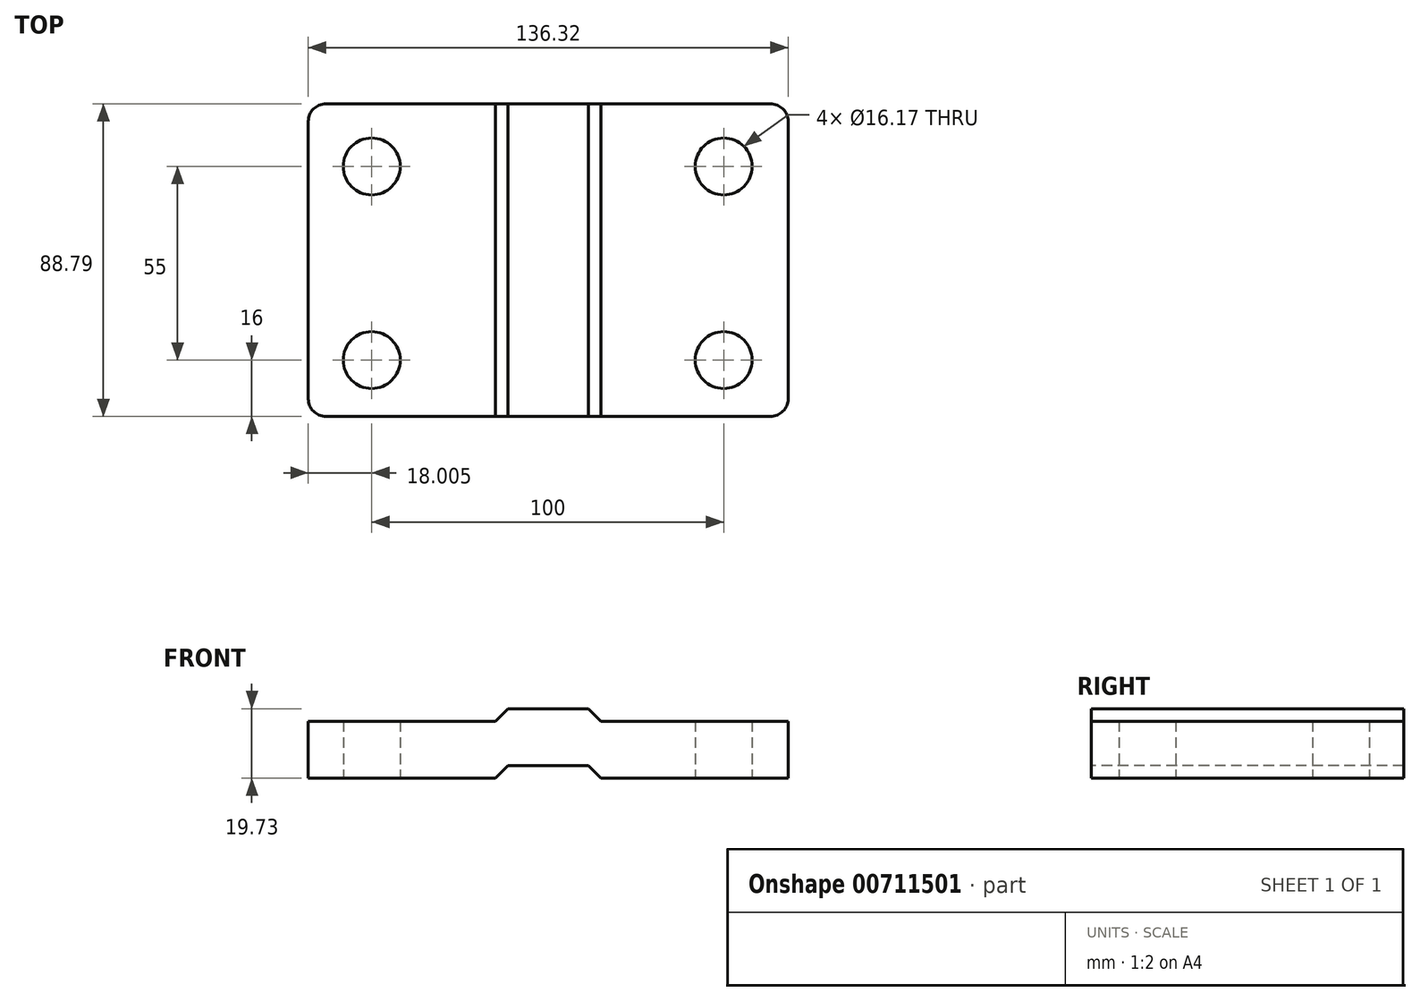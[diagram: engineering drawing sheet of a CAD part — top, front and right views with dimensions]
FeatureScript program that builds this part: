
annotation { "Feature Type Name" : "Feature", "Feature Type Description" : "" }
export const myFeature = defineFeature(function(context is Context, id is Id, definition is map)
    precondition{}
    {
        {
            var Q0;
            Q0=qCreatedBy(makeId("Front.planeOp"),FACE);
            var sketch = newSketch(context, id + "F0", { "sketchPlane" : qUnion([Q0])});
            skLineSegment(sketch, "E0", {"start": v(-68.15, 0) * mm, "end": v(68.16, 0) * mm});
            skLineSegment(sketch, "E1", {"start": v(-68.16, 0) * mm, "end": v(-68.16, 16.17) * mm});
            skLineSegment(sketch, "E2", {"start": v(-68.16, 16.17) * mm, "end": v(68.16, 16.17) * mm});
            skLineSegment(sketch, "E3", {"start": v(68.16, 16.17) * mm, "end": v(68.16, 0) * mm});
            skSolve(sketch);
        }
        {
            var Q0;
            Q0=makeQuery(id+"F0.imprint","IMPRINT",FACE,{"disambiguationData":[TD([[makeQuery(id+"F0.imprint","IMPRINT",EDGE,{"derivedFrom":sQuery(id+"F0.wireOp",EDGE,"E0")}),1.0]])]});
            extrude(context, id + "F1", {"entities" : qUnion([Q0]), "oppositeDirection" : true, "depth" : 88.8 * mm, "offsetDistance" : 25 * mm});
        }
        {
            var Q0;
            Q0=makeQuery(id+"F0.imprint","IMPRINT",FACE,{"disambiguationData":[TD([[makeQuery(id+"F0.imprint","IMPRINT",EDGE,{"derivedFrom":sQuery(id+"F0.wireOp",EDGE,"E0")}),1.0]])]});
            var sketch = newSketch(context, id + "F2", { "sketchPlane" : qUnion([Q0])});
            skLineSegment(sketch, "E4", {"start": v(0, 16.17) * mm, "end": v(-15, 16.17) * mm});
            skLineSegment(sketch, "E5.MirrorCS", {"start": v(0, 16.17) * mm, "end": v(15, 16.17) * mm});
            skLineSegment(sketch, "E6", {"start": v(-15, 16.17) * mm, "end": v(-11.44, 19.72) * mm});
            skLineSegment(sketch, "E7", {"start": v(15, 16.17) * mm, "end": v(11.44, 19.72) * mm});
            skLineSegment(sketch, "E8", {"start": v(-11.45, 19.72) * mm, "end": v(11.44, 19.72) * mm});
            skSolve(sketch);
        }
        {
            var Q0;
            Q0 = qSketchRegion(id + "F2", true);
            extrude(context, id + "F3", {"entities" : qUnion([Q0]), "operationType" : NewBodyOperationType.ADD, "oppositeDirection" : true, "depth" : 88.8 * mm, "offsetDistance" : 25 * mm});
        }
        {
            var Q0;
            Q0=qCreatedBy(makeId("Front.planeOp"),FACE);
            var sketch = newSketch(context, id + "F4", { "sketchPlane" : qUnion([Q0])});
            skLineSegment(sketch, "E9", {"start": v(0, 0) * mm, "end": v(-15, 0) * mm});
            skLineSegment(sketch, "E10.MirrorCS", {"start": v(0, 0) * mm, "end": v(15, 0) * mm});
            skLineSegment(sketch, "E11", {"start": v(-15, 0) * mm, "end": v(-11.46, 3.54) * mm});
            skLineSegment(sketch, "E12", {"start": v(15, 0) * mm, "end": v(11.46, 3.54) * mm});
            skLineSegment(sketch, "E13", {"start": v(-11.46, 3.54) * mm, "end": v(11.46, 3.54) * mm});
            skSolve(sketch);
        }
        {
            var Q0;
            Q0 = qSketchRegion(id + "F4", true);
            extrude(context, id + "F5", {"entities" : qUnion([Q0]), "operationType" : NewBodyOperationType.REMOVE, "oppositeDirection" : true, "depth" : 88.8 * mm, "offsetDistance" : 25 * mm});
        }
        {
            var Q0;
            Q0=makeQuery(id+"F1.opExtrude","CAP_EDGE",EDGE,{"disambiguationData":[OSD([sQuery(id+"F0.wireOp",EDGE,"E3")])],"isStart":false});
            var Q1;
            Q1=makeQuery(id+"F1.opExtrude","CAP_EDGE",EDGE,{"disambiguationData":[OSD([sQuery(id+"F0.wireOp",EDGE,"E1")])],"isStart":false});
            var Q2;
            Q2=makeQuery(id+"F1.opExtrude","CAP_EDGE",EDGE,{"disambiguationData":[OSD([sQuery(id+"F0.wireOp",EDGE,"E3")])],"isStart":true});
            var Q3;
            Q3=makeQuery(id+"F1.opExtrude","CAP_EDGE",EDGE,{"disambiguationData":[OSD([sQuery(id+"F0.wireOp",EDGE,"E1")])],"isStart":true});
            fillet(context, id + "F6", {"entities" : qUnion([Q0, Q1, Q2, Q3]), "radius" : 5 * mm, "tangentPropagation" : true, "allowEdgeOverflow" : false});
        }
        {
            var Q0;
            Q0=qCreatedBy(makeId("Top.planeOp"),FACE);
            var sketch = newSketch(context, id + "F7", { "sketchPlane" : qUnion([Q0])});
            skCircle(sketch, "E14", {"center": v(-50.15, 71) * mm, "radius": 7.5 * mm});
            skCircle(sketch, "E15", {"center": v(-50.16, 16) * mm, "radius": 7.5 * mm});
            skCircle(sketch, "E16", {"center": v(49.85, 71) * mm, "radius": 7.5 * mm});
            skCircle(sketch, "E17", {"center": v(49.85, 16) * mm, "radius": 7.5 * mm});
            skSolve(sketch);
        }
        {
            var Q0;
            Q0=sQuery(id+"F7.wireOp",VERTEX,"E14.center");
            var Q1;
            Q1=sQuery(id+"F7.wireOp",VERTEX,"E15.center");
            var Q2;
            Q2=sQuery(id+"F7.wireOp",VERTEX,"E16.center");
            var Q3;
            Q3=sQuery(id+"F7.wireOp",VERTEX,"E17.center");
            var Q4;
            Q4=makeQuery(id+"F1.opExtrude","SWEPT_BODY",BODY,{"disambiguationData":[OSD([sQuery(id+"F0.wireOp",EDGE,"E0"),sQuery(id+"F0.wireOp",EDGE,"E1"),sQuery(id+"F0.wireOp",EDGE,"E2"),sQuery(id+"F0.wireOp",EDGE,"E3")])]});
            hole(context, id + "F8", {"style" : HoleStyle.SIMPLE, "endStyle" : HoleEndStyle.THROUGH, "oppositeDirection" : true, "holeDiameter" : 16.17 * mm, "majorDiameter" : 14 * mm, "isTappedThrough" : true, "tappedDepth" : 12 * mm, "tapClearance" : 3, "locations" : qUnion([Q0, Q1, Q2, Q3]), "scope" : qUnion([Q4])});
        }
    });
